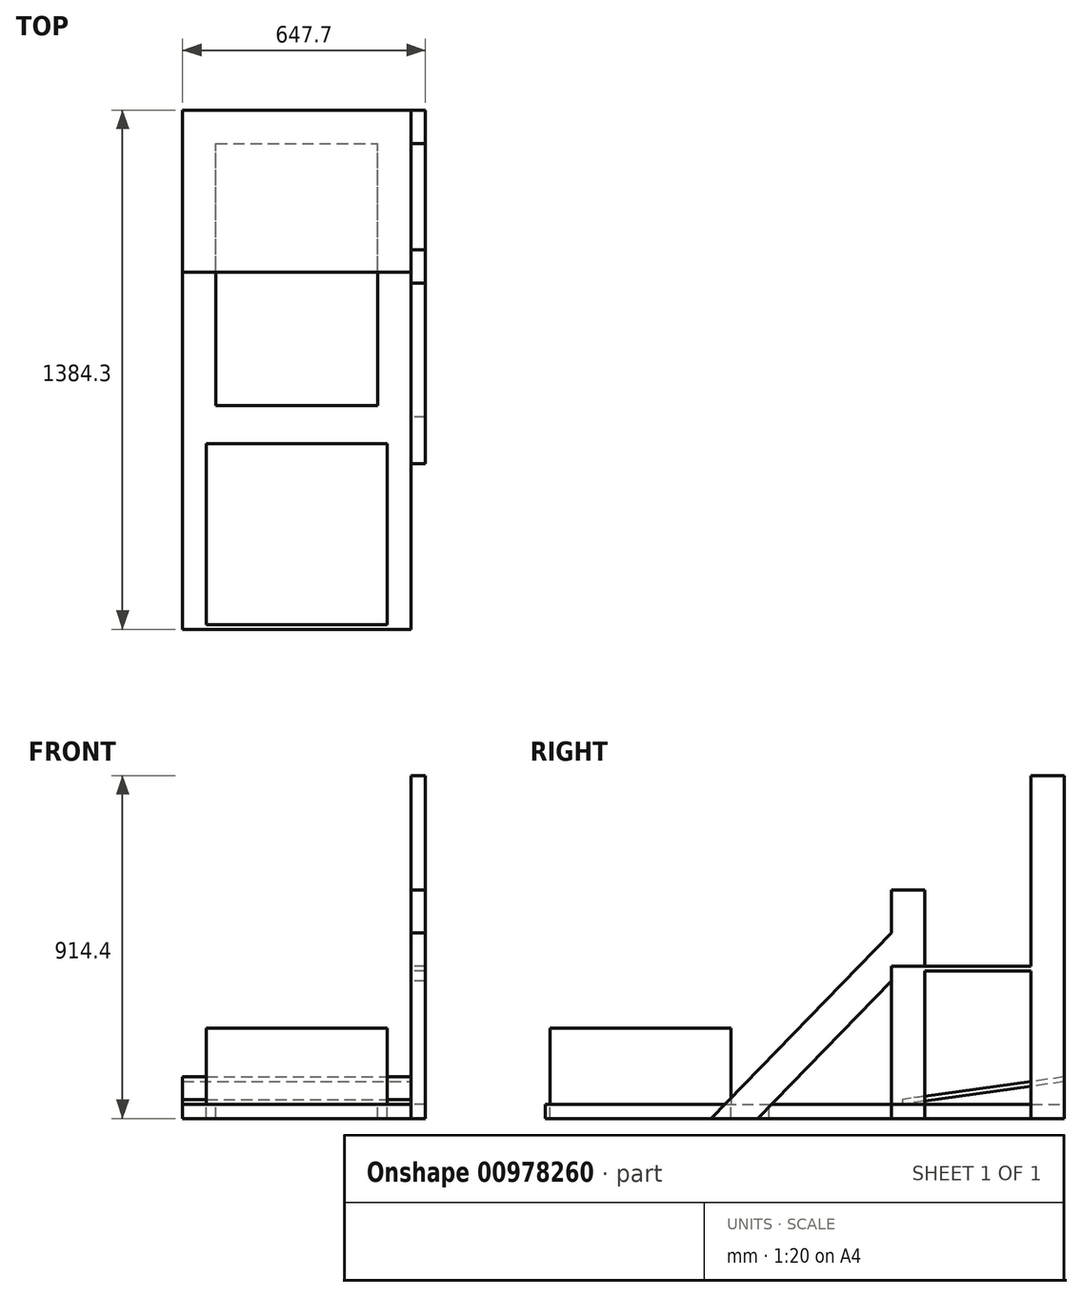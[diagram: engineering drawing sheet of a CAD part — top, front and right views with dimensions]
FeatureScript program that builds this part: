
annotation { "Feature Type Name" : "Feature", "Feature Type Description" : "" }
export const myFeature = defineFeature(function(context is Context, id is Id, definition is map)
    precondition{}
    {
        {
            var Q0;
            Q0=qCreatedBy(makeId("Top.planeOp"),FACE);
            var sketch = newSketch(context, id + "F0", { "sketchPlane" : qUnion([Q0])});
            skLineSegment(sketch, "E0.bottom", {"start": v(0, 0) * mm, "end": v(609.6, 0) * mm});
            skLineSegment(sketch, "E0.top", {"start": v(0, 88.9) * mm, "end": v(609.6, 88.9) * mm});
            skLineSegment(sketch, "E0.left", {"start": v(0, 0) * mm, "end": v(0, 88.9) * mm});
            skLineSegment(sketch, "E0.right", {"start": v(609.6, 0) * mm, "end": v(609.6, 88.9) * mm});
            skLineSegment(sketch, "E1.bottom", {"start": v(0, 88.9) * mm, "end": v(88.9, 88.9) * mm});
            skLineSegment(sketch, "E1.top", {"start": v(0, 876.3) * mm, "end": v(88.9, 876.3) * mm});
            skLineSegment(sketch, "E1.left", {"start": v(0, 88.9) * mm, "end": v(0, 876.3) * mm});
            skLineSegment(sketch, "E1.right", {"start": v(88.9, 88.9) * mm, "end": v(88.9, 876.3) * mm});
            skLineSegment(sketch, "E2.bottom", {"start": v(609.6, 88.9) * mm, "end": v(520.7, 88.9) * mm});
            skLineSegment(sketch, "E2.top", {"start": v(609.6, 876.3) * mm, "end": v(520.7, 876.3) * mm});
            skLineSegment(sketch, "E2.left", {"start": v(609.6, 88.9) * mm, "end": v(609.6, 876.3) * mm});
            skLineSegment(sketch, "E2.right", {"start": v(520.7, 88.9) * mm, "end": v(520.7, 876.3) * mm});
            skLineSegment(sketch, "E3", {"start": v(88.9, 444.5) * mm, "end": v(520.7, 444.5) * mm});
            skLineSegment(sketch, "E4.bottom", {"start": v(88.9, 876.3) * mm, "end": v(520.7, 876.3) * mm});
            skLineSegment(sketch, "E4.top", {"start": v(88.9, 787.4) * mm, "end": v(520.7, 787.4) * mm});
            skLineSegment(sketch, "E4.left", {"start": v(88.9, 876.3) * mm, "end": v(88.9, 787.4) * mm});
            skLineSegment(sketch, "E4.right", {"start": v(520.7, 876.3) * mm, "end": v(520.7, 787.4) * mm});
            skSolve(sketch);
        }
        {
            var Q0;
            Q0 = qSketchRegion(id + "F0", true);
            extrude(context, id + "F1", {"entities" : qUnion([Q0]), "depth" : -38.1 * mm, "offsetDistance" : 25.4 * mm});
        }
        {
            var Q0;
            Q0=makeQuery(id+"F1.opExtrude","SWEPT_FACE",FACE,{"disambiguationData":[OSD([sQuery(id+"F0.wireOp",EDGE,"E2.right")])]});
            var sketch = newSketch(context, id + "F2", { "sketchPlane" : qUnion([Q0])});
            skLineSegment(sketch, "E5", {"start": v(-444.5, 0) * mm, "end": v(-876.3, 0) * mm});
            skLineSegment(sketch, "E6", {"start": v(-876.3, 0) * mm, "end": v(-876.3, 59.84) * mm});
            skLineSegment(sketch, "E7", {"start": v(-876.3, 59.84) * mm, "end": v(-444.5, 0) * mm});
            skLineSegment(sketch, "E8", {"start": v(-876.3, 59.84) * mm, "end": v(-876.3, 72.54) * mm});
            skLineSegment(sketch, "E9", {"start": v(-876.3, 72.54) * mm, "end": v(-444.5, 12.7) * mm});
            skLineSegment(sketch, "E10", {"start": v(-444.5, 12.7) * mm, "end": v(-444.5, 0) * mm});
            skSolve(sketch);
        }
        {
            var Q0;
            Q0=makeQuery(id+"F2.imprint","IMPRINT",FACE,{"disambiguationData":[TD([[makeQuery(id+"F2.imprint","IMPRINT",EDGE,{"derivedFrom":sQuery(id+"F2.wireOp",EDGE,"E7")}),1.0]])]});
            extrude(context, id + "F3", {"entities" : qUnion([Q0]), "depth" : 431.8 * mm, "offsetDistance" : 25.4 * mm});
        }
        {
            var Q0;
            Q0=makeQuery(id+"F3.opExtrude","CAP_FACE",FACE,{"disambiguationData":[OSD([sQuery(id+"F2.wireOp",EDGE,"E7"),sQuery(id+"F2.wireOp",EDGE,"E8"),sQuery(id+"F2.wireOp",EDGE,"E9"),sQuery(id+"F2.wireOp",EDGE,"E10")])],"isStart":true});
            extrude(context, id + "F4", {"entities" : qUnion([Q0]), "operationType" : NewBodyOperationType.ADD, "depth" : 88.9 * mm, "offsetDistance" : 25.4 * mm});
        }
        {
            var Q0;
            Q0=makeQuery(id+"F3.opExtrude","CAP_FACE",FACE,{"disambiguationData":[OSD([sQuery(id+"F2.wireOp",EDGE,"E7"),sQuery(id+"F2.wireOp",EDGE,"E8"),sQuery(id+"F2.wireOp",EDGE,"E9"),sQuery(id+"F2.wireOp",EDGE,"E10")])],"isStart":false});
            extrude(context, id + "F5", {"entities" : qUnion([Q0]), "operationType" : NewBodyOperationType.ADD, "depth" : 88.9 * mm, "offsetDistance" : 25.4 * mm});
        }
        {
            var Q0;
            Q0=qCreatedBy(makeId("Top.planeOp"),FACE);
            var sketch = newSketch(context, id + "F6", { "sketchPlane" : qUnion([Q0])});
            skLineSegment(sketch, "E11.bottom", {"start": v(0, 0) * mm, "end": v(609.6, 0) * mm});
            skLineSegment(sketch, "E11.top", {"start": v(0, -508) * mm, "end": v(609.6, -508) * mm});
            skLineSegment(sketch, "E11.left", {"start": v(0, 0) * mm, "end": v(0, -508) * mm});
            skLineSegment(sketch, "E11.right", {"start": v(609.6, 0) * mm, "end": v(609.6, -508) * mm});
            skLineSegment(sketch, "E12.bottom", {"start": v(63.5, -495.3) * mm, "end": v(546.1, -495.3) * mm});
            skLineSegment(sketch, "E12.top", {"start": v(63.5, -12.7) * mm, "end": v(546.1, -12.7) * mm});
            skLineSegment(sketch, "E12.left", {"start": v(63.5, -495.3) * mm, "end": v(63.5, -12.7) * mm});
            skLineSegment(sketch, "E12.right", {"start": v(546.1, -495.3) * mm, "end": v(546.1, -12.7) * mm});
            skSolve(sketch);
        }
        {
            var Q0;
            Q0=makeQuery(id+"F6.imprint","IMPRINT",FACE,{"disambiguationData":[TD([[makeQuery(id+"F6.imprint","IMPRINT",EDGE,{"derivedFrom":sQuery(id+"F6.wireOp",EDGE,"E12.bottom")}),1.0]])]});
            extrude(context, id + "F7", {"entities" : qUnion([Q0]), "depth" : 203.2 * mm, "offsetDistance" : 25.4 * mm});
        }
        {
            var Q0;
            Q0=makeQuery(id+"F6.imprint","IMPRINT",FACE,{"disambiguationData":[TD([[makeQuery(id+"F6.imprint","IMPRINT",EDGE,{"derivedFrom":sQuery(id+"F6.wireOp",EDGE,"E11.bottom")}),-1.0]])]});
            extrude(context, id + "F8", {"entities" : qUnion([Q0]), "operationType" : NewBodyOperationType.ADD, "depth" : -38.1 * mm, "offsetDistance" : 25.4 * mm});
        }
        {
            var Q0;
            Q0=makeQuery(id+"F8.boolean.opBoolean","MERGE",FACE,{"derivedFrom":[makeQuery(id+"F1.opExtrude","SWEPT_FACE",FACE,{"disambiguationData":[OSD([sQuery(id+"F0.wireOp",EDGE,"E0.right"),sQuery(id+"F0.wireOp",EDGE,"E2.left")])]}),makeQuery(id+"F8.opExtrude","SWEPT_FACE",FACE,{"disambiguationData":[OSD([sQuery(id+"F6.wireOp",EDGE,"E11.right")])]})]});
            var sketch = newSketch(context, id + "F9", { "sketchPlane" : qUnion([Q0])});
            skLineSegment(sketch, "E13.bottom", {"start": v(876.3, -38.1) * mm, "end": v(787.4, -38.1) * mm});
            skLineSegment(sketch, "E13.top", {"start": v(876.3, 876.3) * mm, "end": v(787.4, 876.3) * mm});
            skLineSegment(sketch, "E13.left", {"start": v(876.3, -38.1) * mm, "end": v(876.3, 876.3) * mm});
            skLineSegment(sketch, "E13.right", {"start": v(787.4, -38.1) * mm, "end": v(787.4, 876.3) * mm});
            skLineSegment(sketch, "E14.bottom", {"start": v(415.25, -38.1) * mm, "end": v(504.15, -38.1) * mm});
            skLineSegment(sketch, "E14.top", {"start": v(415.25, 571.5) * mm, "end": v(504.15, 571.5) * mm});
            skLineSegment(sketch, "E14.left", {"start": v(415.25, -38.1) * mm, "end": v(415.25, 571.5) * mm});
            skLineSegment(sketch, "E14.right", {"start": v(504.15, -38.1) * mm, "end": v(504.15, 571.5) * mm});
            skLineSegment(sketch, "E15", {"start": v(-66.45, -38.1) * mm, "end": v(415.25, 456.24) * mm});
            skLineSegment(sketch, "E16", {"start": v(415.25, 456.24) * mm, "end": v(415.25, 328.85) * mm});
            skLineSegment(sketch, "E17", {"start": v(415.25, 328.85) * mm, "end": v(57.68, -38.1) * mm});
            skLineSegment(sketch, "E18", {"start": v(-66.45, -38.1) * mm, "end": v(57.68, -38.1) * mm});
            skLineSegment(sketch, "E19", {"start": v(876.3, 355.6) * mm, "end": v(415.25, 355.6) * mm});
            skLineSegment(sketch, "E20", {"start": v(415.25, 355.6) * mm, "end": v(415.25, 368.3) * mm});
            skLineSegment(sketch, "E21", {"start": v(415.25, 368.3) * mm, "end": v(876.3, 368.3) * mm});
            skLineSegment(sketch, "E22", {"start": v(876.3, 368.3) * mm, "end": v(876.3, 355.6) * mm});
            skSolve(sketch);
        }
        {
            var Q0;
            {var subQ0=sQuery(id+"F9.wireOp",EDGE,"E18");var subQ8=sQuery(id+"F9.wireOp",EDGE,"E17");var subQ11=sQuery(id+"F9.wireOp",EDGE,"E21");var subQ12=sQuery(id+"F9.wireOp",EDGE,"E13.left");var subQ13=makeQuery(id+"F9.imprint","INTERSECT",VERTEX,{"derivedFrom":[subQ12,subQ11]});var subQ14=sQuery(id+"F9.wireOp",EDGE,"E19");var subQ16=sQuery(id+"F9.wireOp",EDGE,"E13.right");var subQ17=makeQuery(id+"F9.imprint","INTERSECT",VERTEX,{"derivedFrom":[subQ16,subQ11]});var subQ18=makeQuery(id+"F9.imprint","INTERSECT",VERTEX,{"derivedFrom":[subQ16,subQ14]});var subQ19=makeQuery(id+"F9.imprint","IMPRINT",EDGE,{"disambiguationData":[TD([[subQ17,1.0]])],"derivedFrom":subQ16});var subQ20=makeQuery(id+"F9.imprint","IMPRINT",EDGE,{"disambiguationData":[TD([[subQ18,1.0]])],"derivedFrom":subQ14});var subQ22=sQuery(id+"F9.wireOp",EDGE,"E14.left");var subQ24=makeQuery(id+"F9.imprint","INTERSECT",VERTEX,{"derivedFrom":[subQ22,subQ11]});var subQ26=makeQuery(id+"F9.imprint","IMPRINT",EDGE,{"disambiguationData":[TD([[subQ24,1.0]])],"derivedFrom":subQ22});var subQ27=makeQuery(id+"F9.imprint","INTERSECT",VERTEX,{"derivedFrom":[subQ22,subQ8]});var subQ28=makeQuery(id+"F9.imprint","IMPRINT",EDGE,{"disambiguationData":[TD([[subQ27,-1.0]])],"derivedFrom":subQ22});var subQ29=makeQuery(id+"F9.imprint","IMPRINT",EDGE,{"disambiguationData":[TD([[subQ24,-1.0]])],"derivedFrom":subQ22});var subQ30=sQuery(id+"F9.wireOp",EDGE,"E13.bottom");var subQ35=sQuery(id+"F9.wireOp",EDGE,"E14.top");var subQ43=sQuery(id+"F9.wireOp",EDGE,"E14.bottom");var subQ45=sQuery(id+"F9.wireOp",EDGE,"E13.top");Q0=qUnion([makeQuery(id+"F9.imprint","IMPRINT",FACE,{"disambiguationData":[TD([[subQ19,1.0]])]}),makeQuery(id+"F9.imprint","IMPRINT",FACE,{"disambiguationData":[TD([[subQ20,1.0]])]}),makeQuery(id+"F9.imprint","IMPRINT",FACE,{"disambiguationData":[TD([[makeQuery(id+"F9.imprint","IMPRINT",EDGE,{"derivedFrom":subQ45}),1.0]])]}),makeQuery(id+"F9.imprint","IMPRINT",FACE,{"disambiguationData":[TD([[subQ26,-1.0]])]}),makeQuery(id+"F9.imprint","IMPRINT",FACE,{"disambiguationData":[TD([[makeQuery(id+"F9.imprint","IMPRINT",EDGE,{"derivedFrom":subQ43}),1.0]])]}),makeQuery(id+"F9.imprint","IMPRINT",FACE,{"disambiguationData":[TD([[subQ28,-1.0]])]}),makeQuery(id+"F9.imprint","IMPRINT",FACE,{"disambiguationData":[TD([[makeQuery(id+"F9.imprint","IMPRINT",EDGE,{"derivedFrom":subQ35}),-1.0]])]}),makeQuery(id+"F9.imprint","IMPRINT",FACE,{"disambiguationData":[TD([[makeQuery(id+"F9.imprint","IMPRINT",EDGE,{"derivedFrom":subQ30}),1.0]])]}),makeQuery(id+"F9.imprint","IMPRINT",FACE,{"disambiguationData":[TD([[subQ29,1.0]])]}),makeQuery(id+"F9.imprint","IMPRINT",FACE,{"disambiguationData":[TD([[makeQuery(id+"F9.imprint","IMPRINT",EDGE,{"disambiguationData":[TD([[subQ13,1.0]])],"derivedFrom":subQ12}),1.0]])]}),makeQuery(id+"F9.imprint","IMPRINT",FACE,{"disambiguationData":[TD([[makeQuery(id+"F9.imprint","IMPRINT",EDGE,{"derivedFrom":subQ0}),1.0]])]})]);}
            extrude(context, id + "F10", {"entities" : qUnion([Q0]), "depth" : 38.1 * mm, "offsetDistance" : 25.4 * mm});
        }
        {
            var Q0;
            {var subQ1=sQuery(id+"F9.wireOp",EDGE,"E14.left");var subQ5=makeQuery(id+"F9.imprint","INTERSECT",VERTEX,{"derivedFrom":[subQ1,sQuery(id+"F9.wireOp",EDGE,"E21")]});Q0=makeQuery(id+"F9.imprint","IMPRINT",FACE,{"disambiguationData":[TD([[makeQuery(id+"F9.imprint","IMPRINT",EDGE,{"disambiguationData":[TD([[subQ5,-1.0]])],"derivedFrom":subQ1}),1.0]])]});}
            var Q1;
            {var subQ0=sQuery(id+"F9.wireOp",EDGE,"E18");Q1=makeQuery(id+"F9.imprint","IMPRINT",FACE,{"disambiguationData":[TD([[makeQuery(id+"F9.imprint","IMPRINT",EDGE,{"derivedFrom":subQ0}),1.0]])]});}
            var Q2;
            {var subQ1=sQuery(id+"F9.wireOp",EDGE,"E14.top");Q2=makeQuery(id+"F9.imprint","IMPRINT",FACE,{"disambiguationData":[TD([[makeQuery(id+"F9.imprint","IMPRINT",EDGE,{"derivedFrom":subQ1}),-1.0]])]});}
            var Q3;
            {var subQ0=sQuery(id+"F9.wireOp",EDGE,"E14.bottom");Q3=makeQuery(id+"F9.imprint","IMPRINT",FACE,{"disambiguationData":[TD([[makeQuery(id+"F9.imprint","IMPRINT",EDGE,{"derivedFrom":subQ0}),1.0]])]});}
            extrude(context, id + "F11", {"entities" : qUnion([Q0, Q1, Q2, Q3]), "depth" : 38.1 * mm, "offsetDistance" : 25.4 * mm});
        }
    });
